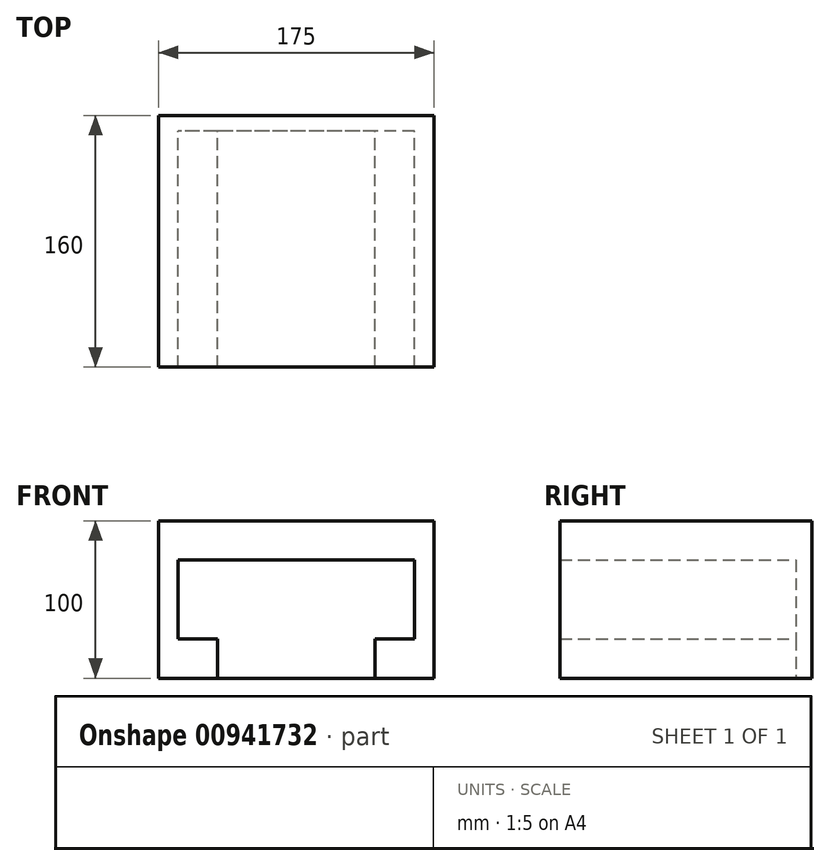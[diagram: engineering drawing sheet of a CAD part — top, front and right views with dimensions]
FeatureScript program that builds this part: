
annotation { "Feature Type Name" : "Feature", "Feature Type Description" : "" }
export const myFeature = defineFeature(function(context is Context, id is Id, definition is map)
    precondition{}
    {
        {
            var Q0;
            Q0=qCreatedBy(makeId("Front.planeOp"),FACE);
            var sketch = newSketch(context, id + "F0", { "sketchPlane" : qUnion([Q0])});
            skLineSegment(sketch, "E0.bottom", {"start": v(87.5, 50) * mm, "end": v(-87.5, 50) * mm});
            skLineSegment(sketch, "E0.top", {"start": v(87.5, -50) * mm, "end": v(-87.5, -50) * mm});
            skLineSegment(sketch, "E0.left", {"start": v(87.5, 50) * mm, "end": v(87.5, -50) * mm});
            skLineSegment(sketch, "E0.right", {"start": v(-87.5, 50) * mm, "end": v(-87.5, -50) * mm});
            skPoint(sketch, "E0.middle", {"position": v(0, 0) * mm});
            skLineSegment(sketch, "E1.bottom", {"start": v(75, 25) * mm, "end": v(-75, 25) * mm});
            skLineSegment(sketch, "E1.top", {"start": v(75, -25) * mm, "end": v(-75, -25) * mm});
            skLineSegment(sketch, "E1.left", {"start": v(75, 25) * mm, "end": v(75, -25) * mm});
            skLineSegment(sketch, "E1.right", {"start": v(-75, 25) * mm, "end": v(-75, -25) * mm});
            skLineSegment(sketch, "E2", {"start": v(-50, -25) * mm, "end": v(-50, -50) * mm});
            skLineSegment(sketch, "E3", {"start": v(50, -25) * mm, "end": v(50, -50) * mm});
            skLineSegment(sketch, "E4", {"start": v(50, -25) * mm, "end": v(75, -25) * mm});
            skLineSegment(sketch, "E5", {"start": v(-50, -25) * mm, "end": v(-75, -25) * mm});
            skSolve(sketch);
        }
        {
            var Q0;
            Q0=makeQuery(id+"F0.imprint","IMPRINT",FACE,{"disambiguationData":[TD([[makeQuery(id+"F0.imprint","IMPRINT",EDGE,{"derivedFrom":sQuery(id+"F0.wireOp",EDGE,"E0.bottom")}),1.0]])]});
            extrude(context, id + "F1", {"entities" : qUnion([Q0]), "depth" : 75 * mm, "offsetDistance" : 25 * mm, "hasSecondDirection" : true, "secondDirectionOppositeDirection" : true, "secondDirectionDepth" : 75 * mm});
        }
        {
            var Q0;
            Q0=makeQuery(id+"F1.opExtrude","CAP_FACE",FACE,{"disambiguationData":[OSD([sQuery(id+"F0.wireOp",EDGE,"E0.bottom"),sQuery(id+"F0.wireOp",EDGE,"E0.top"),sQuery(id+"F0.wireOp",EDGE,"E0.left"),sQuery(id+"F0.wireOp",EDGE,"E0.right"),sQuery(id+"F0.wireOp",EDGE,"E1.bottom"),sQuery(id+"F0.wireOp",EDGE,"E1.top"),sQuery(id+"F0.wireOp",EDGE,"E1.left"),sQuery(id+"F0.wireOp",EDGE,"E1.right"),sQuery(id+"F0.wireOp",EDGE,"E2"),sQuery(id+"F0.wireOp",EDGE,"E3")])],"isStart":true});
            var sketch = newSketch(context, id + "F2", { "sketchPlane" : qUnion([Q0])});
            skLineSegment(sketch, "E6.bottom", {"start": v(-87.5, 50) * mm, "end": v(87.5, 50) * mm});
            skLineSegment(sketch, "E6.top", {"start": v(-87.5, -50) * mm, "end": v(87.5, -50) * mm});
            skLineSegment(sketch, "E6.left", {"start": v(-87.5, 50) * mm, "end": v(-87.5, -50) * mm});
            skLineSegment(sketch, "E6.right", {"start": v(87.5, 50) * mm, "end": v(87.5, -50) * mm});
            skSolve(sketch);
        }
        {
            var Q0;
            Q0 = qSketchRegion(id + "F2", true);
            extrude(context, id + "F3", {"entities" : qUnion([Q0]), "operationType" : NewBodyOperationType.ADD, "depth" : 10 * mm, "offsetDistance" : 25 * mm});
        }
    });
